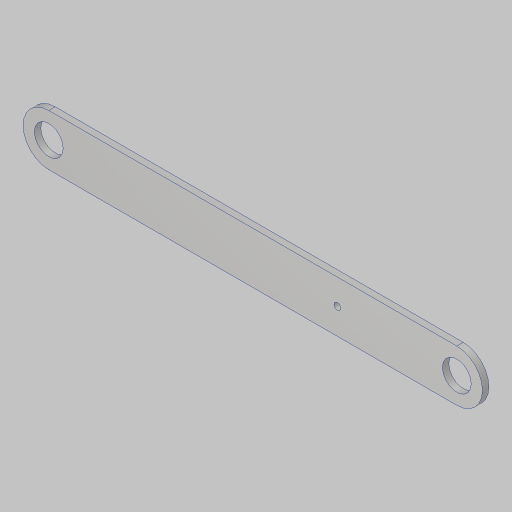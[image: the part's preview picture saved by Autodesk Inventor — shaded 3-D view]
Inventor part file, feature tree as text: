
AUTODESK INVENTOR PART (.ipt)
format: ipt  version: 2023.5 (Build 275446000, 446)  size: 102,912 bytes
history: native  units: in
note: dims shown in document units (in); Inventor stores cm internally (conversion verified against a paired STEP export)
features: sketch x1, extrude x1, hole x1
ambient origin geometry x8: Origin, YZ Plane, XZ Plane, XY Plane, X Axis, Y Axis, Z Axis, Center Point
bodies: Solid1 (feature_tree)
feature tree (3):
  sketch  "Sketch1"  dims[d0=1.125in d1=15.907in d2=2.0in d3=11.25in d5=0.25in d6=0.0in d7=0.266in d8=0.75in d9=0.507in d10=0.25in d11=0.5635in d12=1.0in d13=0.8108in d14=0.012in]
  extrude  "Extrusion1"  Depth=15.907in
  hole  "Hole1"  [1 undecoded]
note: 1 required parameter value undecoded (feature->parameter linkage not recoverable at this tier; creation-order binding heuristic only, values carry confidence <= 0.55)
